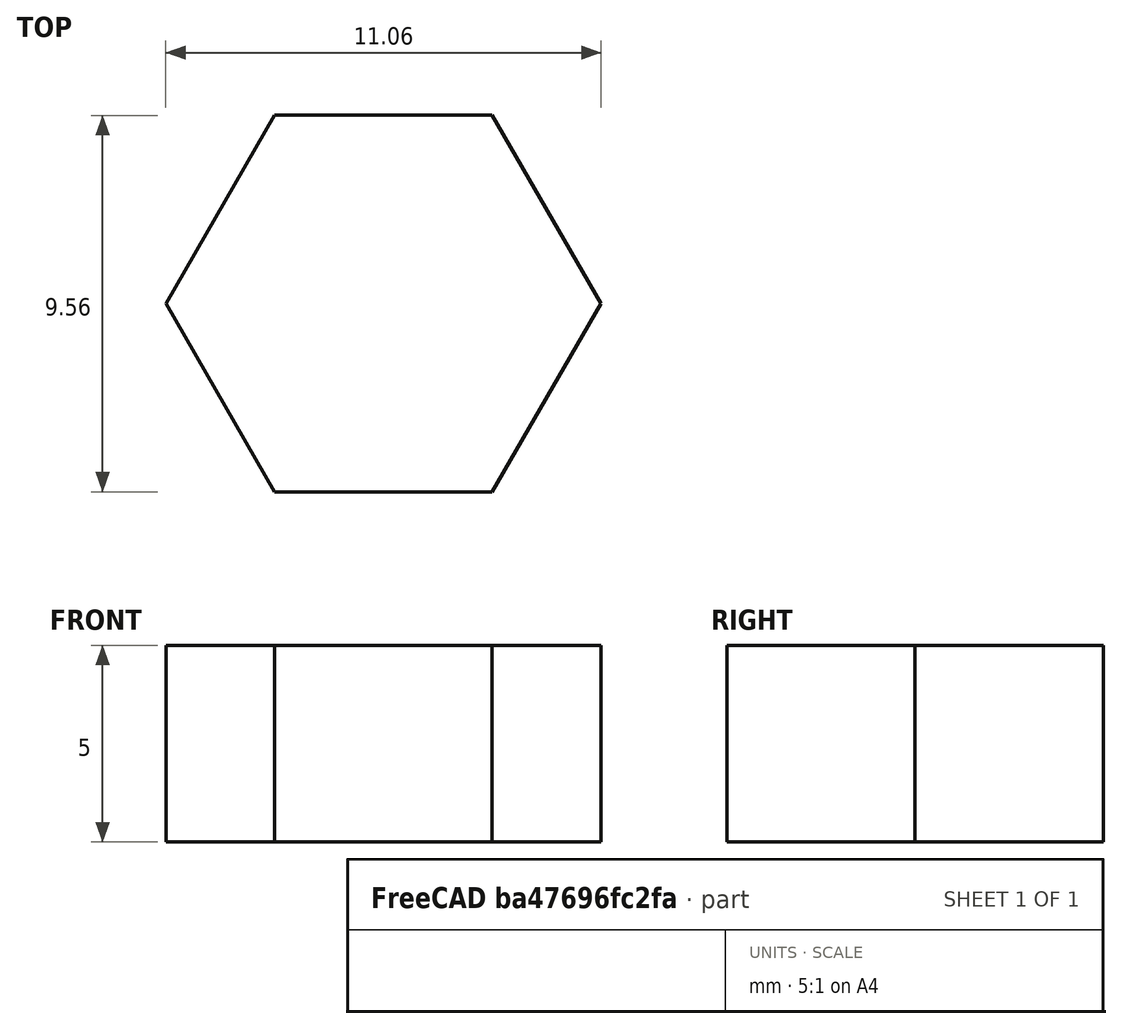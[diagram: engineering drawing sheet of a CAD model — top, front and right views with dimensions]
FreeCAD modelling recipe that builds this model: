
FCSTD DOCUMENT  (FreeCAD 0.21R0.20.1)
Label: Nut_DIN934_M6
License: All rights reserved
LicenseURL: https://en.wikipedia.org/wiki/All_rights_reserved
objects: Sketcher::SketchObject×1, Part::Extrusion×1
note: 2 computed .brp shape members not serialized (recipe doc carries the construction recipe); baked Part::Feature solids carry a one-line shape summary decoded from their .brp

FEATURE [Sketcher::SketchObject] Sketch
  FullyConstrained = true
  sketch-geometry (7):
    g0: LineSegment StartX=-5.525 StartY=0 StartZ=0 EndX=-2.7625 EndY=-4.78479 EndZ=0
    g1: LineSegment StartX=-2.7625 StartY=-4.78479 StartZ=0 EndX=2.7625 EndY=-4.78479 EndZ=0
    g2: LineSegment StartX=2.7625 StartY=-4.78479 StartZ=0 EndX=5.525 EndY=0 EndZ=0
    g3: LineSegment StartX=5.525 StartY=0 StartZ=0 EndX=2.7625 EndY=4.78479 EndZ=0
    g4: LineSegment StartX=2.7625 StartY=4.78479 StartZ=0 EndX=-2.7625 EndY=4.78479 EndZ=0
    g5: LineSegment StartX=-2.7625 StartY=4.78479 StartZ=0 EndX=-5.525 EndY=0 EndZ=0
    g6: Circle CenterX=0 CenterY=0 CenterZ=0 NormalX=0 NormalY=0 NormalZ=1 AngleXU=0 Radius=5.525
  constraints (16):
    c: Coincident(g0,g1)
    c: Coincident(g1,g2)
    c: Coincident(g2,g3)
    c: Coincident(g3,g4)
    c: Coincident(g4,g5)
    c: Coincident(g5,g0)
    c: Equal(g0, g1-g5) x5
    c: PointOnObject(g0,g6)
    c: PointOnObject(g1,g6)
    c: PointOnObject(g2,g6)
    c: PointOnObject(g3,g6)
    c: PointOnObject(g4,g6)
    c: PointOnObject(g5,g6)
    c: Coincident(g6,g-1)
    c: PointOnObject(g5,g-1)
    c: DistanceX(g0,g2) = 11.05
FEATURE [Part::Extrusion] Extrude  label="DIN934_M6"
  Base = -> Sketch
  Dir = (0,0,1)
  DirMode = 2
  FaceMakerClass = Part::FaceMakerBullseye
  LengthFwd = 5
  LengthRev = 0
  Solid = true
  Symmetric = false
